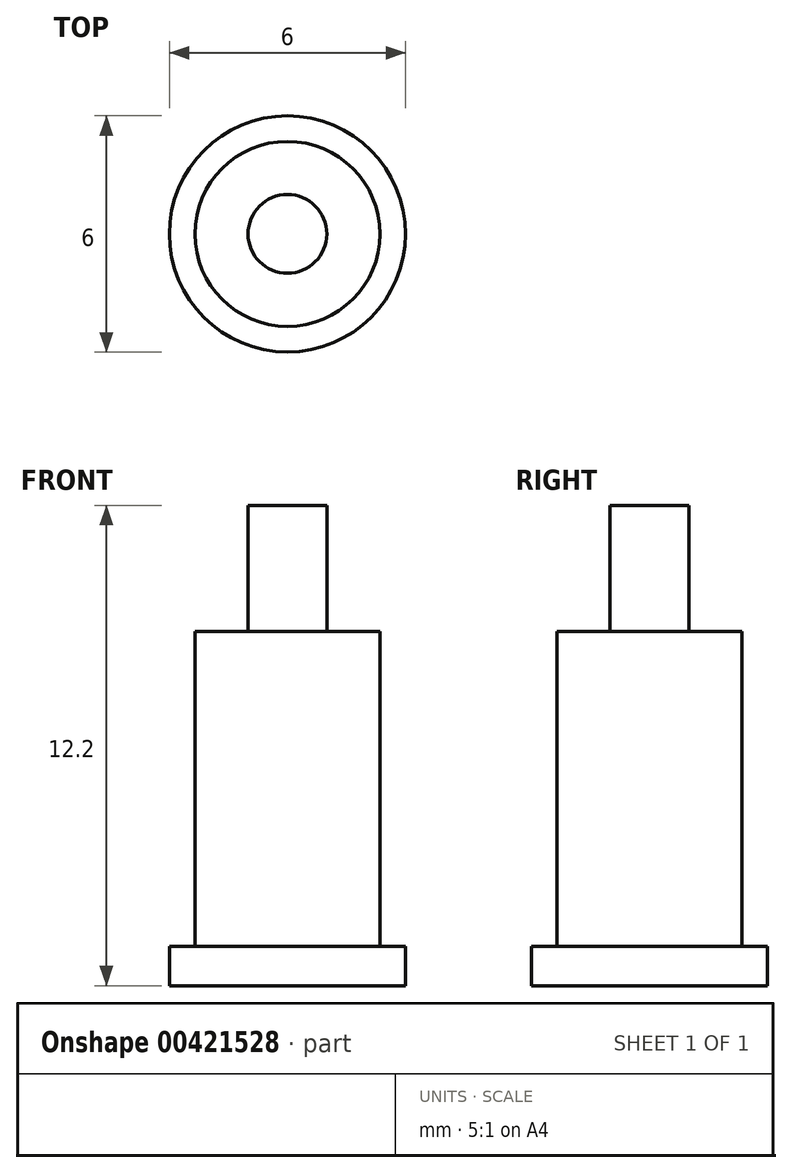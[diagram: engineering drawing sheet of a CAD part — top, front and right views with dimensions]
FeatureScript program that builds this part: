
annotation { "Feature Type Name" : "Feature", "Feature Type Description" : "" }
export const myFeature = defineFeature(function(context is Context, id is Id, definition is map)
    precondition{}
    {
        {
            var Q0;
            Q0=qCreatedBy(makeId("Top.planeOp"),FACE);
            var sketch = newSketch(context, id + "F0", { "sketchPlane" : qUnion([Q0])});
            skCircle(sketch, "E0", {"center": v(0, 0) * mm, "radius": 3 * mm});
            skSolve(sketch);
        }
        {
            var Q0;
            Q0 = qSketchRegion(id + "F0", true);
            extrude(context, id + "F1", {"entities" : qUnion([Q0]), "depth" : 1 * mm, "offsetDistance" : 25 * mm});
        }
        {
            var Q0;
            Q0=makeQuery(id+"F1.opExtrude","CAP_FACE",FACE,{"disambiguationData":[OSD([sQuery(id+"F0.wireOp",EDGE,"E0")])],"isStart":false});
            var sketch = newSketch(context, id + "F2", { "sketchPlane" : qUnion([Q0])});
            skCircle(sketch, "E1", {"center": v(0, 0) * mm, "radius": 2.35 * mm});
            skSolve(sketch);
        }
        {
            var Q0;
            Q0=makeQuery(id+"F2.imprint","IMPRINT",FACE,{"disambiguationData":[TD([[makeQuery(id+"F2.imprint","IMPRINT",EDGE,{"derivedFrom":sQuery(id+"F2.wireOp",EDGE,"E1")}),1.0]])]});
            var Q1;
            Q1=sQuery(id+"F2.wireOp",EDGE,"E1");
            extrude(context, id + "F3", {"entities" : qUnion([Q0]), "operationType" : NewBodyOperationType.ADD, "surfaceEntities" : qUnion([Q1]), "depth" : 8 * mm, "offsetDistance" : 25 * mm});
        }
        {
            var Q0;
            Q0=makeQuery(id+"F3.opExtrude","CAP_FACE",FACE,{"disambiguationData":[OSD([sQuery(id+"F2.wireOp",EDGE,"E1")])],"isStart":false});
            var sketch = newSketch(context, id + "F4", { "sketchPlane" : qUnion([Q0])});
            skCircle(sketch, "E2", {"center": v(0, 0) * mm, "radius": 1 * mm});
            skSolve(sketch);
        }
        {
            var Q0;
            Q0=makeQuery(id+"F4.imprint","IMPRINT",FACE,{"disambiguationData":[TD([[makeQuery(id+"F4.imprint","IMPRINT",EDGE,{"derivedFrom":sQuery(id+"F4.wireOp",EDGE,"E2")}),1.0]])]});
            extrude(context, id + "F5", {"entities" : qUnion([Q0]), "operationType" : NewBodyOperationType.ADD, "depth" : 3.2 * mm, "offsetDistance" : 25 * mm});
        }
    });
